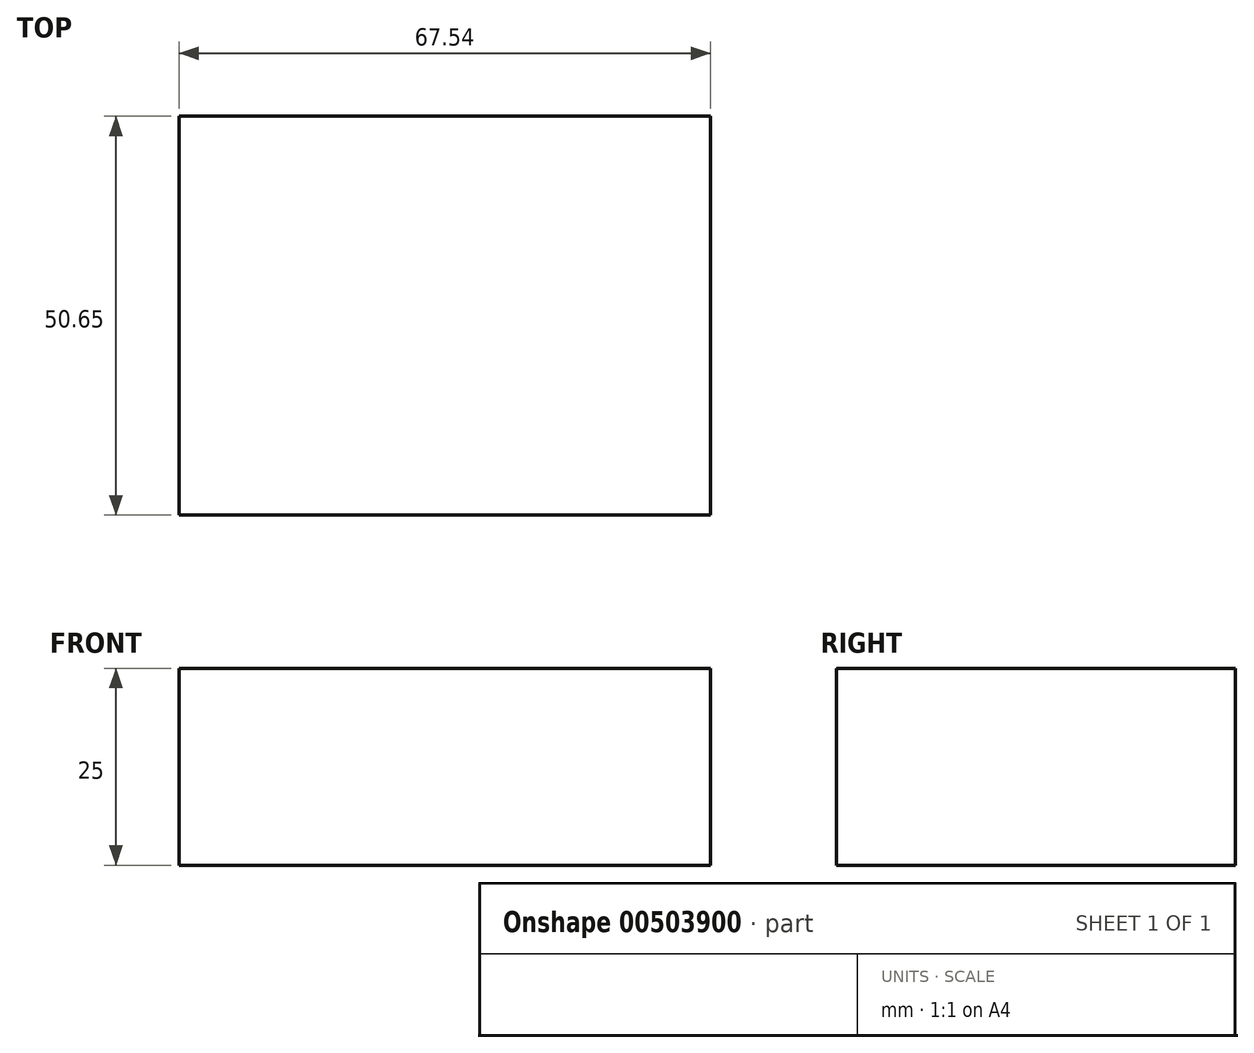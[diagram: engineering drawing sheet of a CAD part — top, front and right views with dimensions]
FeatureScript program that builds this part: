
annotation { "Feature Type Name" : "Feature", "Feature Type Description" : "" }
export const myFeature = defineFeature(function(context is Context, id is Id, definition is map)
    precondition{}
    {
        {
            var Q0;
            Q0=qCreatedBy(makeId("Top.planeOp"),FACE);
            var sketch = newSketch(context, id + "F0", { "sketchPlane" : qUnion([Q0])});
            skLineSegment(sketch, "E0.bottom", {"start": v(-35.62, 32.58) * mm, "end": v(31.92, 32.58) * mm});
            skLineSegment(sketch, "E0.top", {"start": v(-35.62, -18.07) * mm, "end": v(31.92, -18.07) * mm});
            skLineSegment(sketch, "E0.left", {"start": v(-35.62, 32.58) * mm, "end": v(-35.62, -18.07) * mm});
            skLineSegment(sketch, "E0.right", {"start": v(31.92, 32.58) * mm, "end": v(31.92, -18.07) * mm});
            skSolve(sketch);
        }
        {
            var Q0;
            Q0=makeQuery(id+"F0.imprint","IMPRINT",FACE,{"disambiguationData":[TD([[makeQuery(id+"F0.imprint","IMPRINT",EDGE,{"derivedFrom":sQuery(id+"F0.wireOp",EDGE,"E0.bottom")}),-1.0]])]});
            extrude(context, id + "F1", {"entities" : qUnion([Q0]), "depth" : 25 * mm});
        }
    });
